# Revit family: IS_iLifeA_T5247_BIM_GB
name_source: partatom
category: Plumbing Fixtures
units: mm (PartAtom-declared; Revit-internal decimal feet)

## family parameters
Always vertical = No
Cut with Voids When Loaded = No
OmniClass Number = 23.45.05.21.11.11
OmniClass Title = Water Operated Water Closets
Part Type = Normal
Room Calculation Point = No
Round Connector Dimension = Use Diameter
Shared = No
Work Plane-Based = No

## types (1)
- T524701 - Ideal Standard i.life A cistern, side inlet, trim mounted, pre-adjusted, 4.5/3 l, white
    Accessories = https://www.idealstandard.co.uk
    AreaUnits = millimetres
    AssetType = fixed
    BIMObjectName = IS_IdealStandard_WCcisterns_i.lifeA_T5247
    BIMobject category = Toilet Cisterns
    BIMobject category code = toilet-cisterns
    BIMobject main category = Sanitary
    BIMobject main category code = sanitary
    BarCode = 8014140487012
    Brand = Ideal Standard
    Brand url = http://www.idealstandard.co.uk
    CisternCapacity = 0.00 m³
    CisternColor = White
    CisternMaterial = Ceramics
    Color = White
    ConnectionType = Plumbing
    CurrencyUnit = £
    CurrentRevision = 1
    Date of publishing = 07/10/2022
    Description = Cistern, side inlet, trim mounted, pre-adjusted, 4.5/3 l, white
    DurationUnit = years
    Edition number = 1
    ElementType = fixed
    ExpectedLife = 99
    Features = Cistern, side inlet, trim mounted, pre-adjusted, 4.5/3 l, white
    Finish = White
    FlushRate = 0.00 m³
    FlushingRate = 0
    GTIN code = https://8014140487012
    Help = https://www.idealstandard.co.uk
    IFC Classification = Sanitary Terminal
    IfcExportAs = IfcSanitaryTerminalType
    IfcExportType = WASHHANDBASIN
    Installation instructions = https://www.idealstandard.co.uk
    InstallationDate = n /a
    InstallationInstructions = https://www.idealstandard.co.uk
    LinearUnits = millimetres
    MainColor = White
    MaintenanceInformation = https://www.idealstandard.co.uk
    Manufacturer = Ideal Standard
    Manufacturer name = Ideal Standard
    ManufacturerURL = https://www.idealstandard.co.uk
    Masterformat 2014 Code = 22 40 00
    Masterformat 2014 Description = Plumbing Fixtures
    Material = Ceramics
    Material main = Ceramics
    Model = T524701
    ModelNumber = T524701
    ModelReference = I.life A Cistern, side inlet, trim mounted, pre-adjusted, 4.5/3 l, white
    NBS Reference Code = 45-35-70/383
    NBS Reference Description = WC cisterns
    Name = WCcisterns_i.lifeA_T5247_IdealStandard
    NettWeight = 11.4
    NominalDepth = 164 mm
    NominalHeight = 394 mm
    NominalWidth = 355 mm
    OmniClass Code = 23-31 19 00
    OmniClass Description = Toilets
    Product Guid = dd76cc73-859f-474f-9038-35545d76cd66
    Product SKU = T5247
    Product certification = https://www.idealstandard.co.uk
    Product data url = https://bimobject.com
    Product family = I.life A
    Product group = WC Cistern
    Product name = IDEAL STANDARD I.LIFE A CISTERN, SIDE INLET, TRIM MOUNTED, PRE-ADJUSTED, 4.5/3 L
    Product url = https://www.idealstandard.co.uk
    ProductInformation = https://www.idealstandard.co.uk
    QR code = http://bimobject.com
    Shape = sculptured
    Size = 355 x 164 x 394 mm
    Space = Internal
    SpareParts = https://www.idealstandard.co.uk
    Technical description = https://www.idealstandard.co.uk
    UNSPSC Code = 301815
    URL = https://www.idealstandard.co.uk
    Uniclass 1.4 Code = L72164
    Uniclass 1.4 Description = WC Cisterns
    Uniclass 2.0 Code = Pr_40_35_93_90
    Uniclass 2.0 Description = Wc Cisterns
    Uniclass 2015 Code = Pr_40_20_93_89
    Uniclass 2015 Name = WC cisterns
    Uniclass2015Code = Pr_40_20_93_89
    Uniclass2015Title = WC cisterns
    Uniclass2015Version = v1.27
    Uniformat II Code = D2010
    Uniformat II Description = Plumbing Fixtures
    Version = 1
    VolumeUnits = liters
    WRASURL = https://www.wrasapprovals.co.uk
    WarrantyDescription = manufacturer warranty
    WarrantyDurationUnit = years
    Weight Net (Kg) = 11.4
    Youtube clip = https://www.wrasapprovals.co.uk

## geometry (parser evidence)
native form markers: Sweep x1
no freeform markers — native parametric forms only
